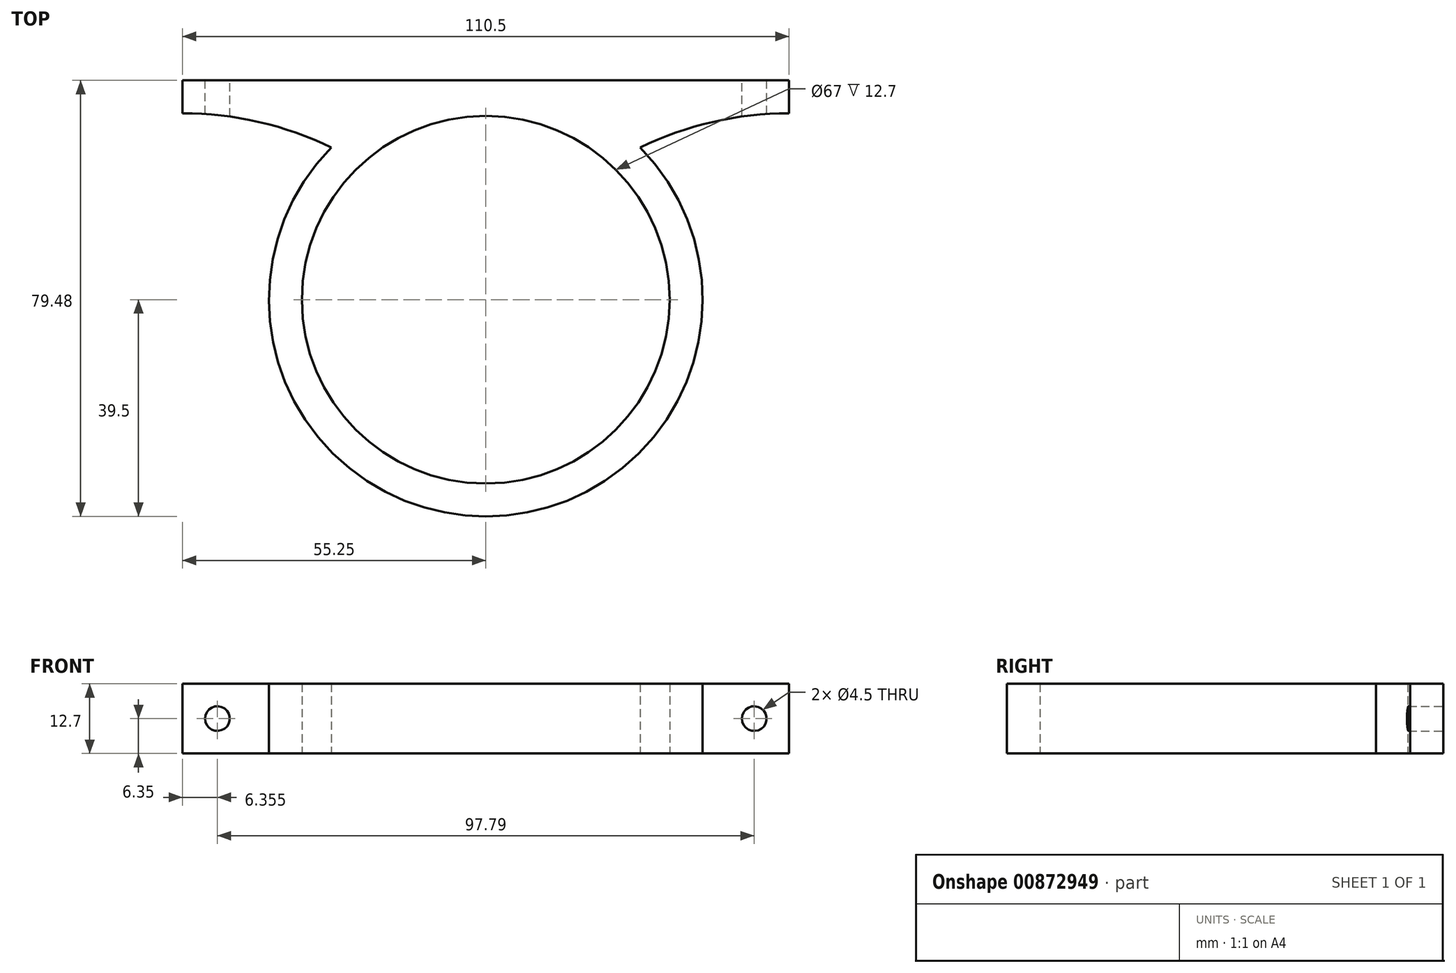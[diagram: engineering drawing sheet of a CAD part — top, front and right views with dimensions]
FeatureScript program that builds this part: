
annotation { "Feature Type Name" : "Feature", "Feature Type Description" : "" }
export const myFeature = defineFeature(function(context is Context, id is Id, definition is map)
    precondition{}
    {
        {
            var Q0;
            Q0=qCreatedBy(makeId("Top.planeOp"),FACE);
            var sketch = newSketch(context, id + "F0", { "sketchPlane" : qUnion([Q0])});
            skCircle(sketch, "E0", {"center": v(0, 0) * mm, "radius": 33.5 * mm});
            skCircle(sketch, "E1", {"center": v(0, 0) * mm, "radius": 39.5 * mm});
            skLineSegment(sketch, "E2.bottom", {"start": v(55.25, 33.98) * mm, "end": v(-55.25, 33.98) * mm});
            skLineSegment(sketch, "E2.top", {"start": v(55.25, 39.98) * mm, "end": v(-55.25, 39.98) * mm});
            skLineSegment(sketch, "E2.left", {"start": v(55.25, 33.98) * mm, "end": v(55.25, 39.98) * mm});
            skLineSegment(sketch, "E2.right", {"start": v(-55.25, 33.98) * mm, "end": v(-55.25, 39.98) * mm});
            skPoint(sketch, "E2.middle", {"position": v(0, 36.98) * mm});
            skArc(sketch, "E3", {"start": v(0, 0) * mm, "mid": v(-22.81, 24.8) * mm, "end": v(-55.24, 33.98) * mm});
            skArc(sketch, "E4", {"start": v(55.25, 33.98) * mm, "mid": v(22.81, 24.8) * mm, "end": v(0, 0) * mm});
            skSolve(sketch);
        }
        {
            var Q0;
            Q0=makeQuery(id+"F0.imprint","IMPRINT",FACE,{"disambiguationData":[TD([[makeQuery(id+"F0.imprint","IMPRINT",EDGE,{"derivedFrom":sQuery(id+"F0.wireOp",EDGE,"E2.top")}),1.0]])]});
            var Q1;
            {var subQ0=sQuery(id+"F0.wireOp",EDGE,"E3");var subQ1=sQuery(id+"F0.wireOp",EDGE,"E1");var subQ2=makeQuery(id+"F0.imprint","INTERSECT",VERTEX,{"derivedFrom":[subQ1,subQ0]});Q1=makeQuery(id+"F0.imprint","IMPRINT",FACE,{"disambiguationData":[TD([[makeQuery(id+"F0.imprint","IMPRINT",EDGE,{"disambiguationData":[TD([[subQ2,1.0]])],"derivedFrom":subQ1}),-1.0]])]});}
            var Q2;
            {var subQ0=sQuery(id+"F0.wireOp",EDGE,"E3");var subQ8=sQuery(id+"F0.wireOp",EDGE,"E0");var subQ9=makeQuery(id+"F0.imprint","INTERSECT",VERTEX,{"derivedFrom":[subQ8,subQ0]});Q2=makeQuery(id+"F0.imprint","IMPRINT",FACE,{"disambiguationData":[TD([[makeQuery(id+"F0.imprint","IMPRINT",EDGE,{"disambiguationData":[TD([[subQ9,1.0]])],"derivedFrom":subQ8}),-1.0]])]});}
            var Q3;
            {var subQ0=sQuery(id+"F0.wireOp",EDGE,"E2.bottom");var subQ1=sQuery(id+"F0.wireOp",EDGE,"E1");var subQ2=makeQuery(id+"F0.imprint","INTERSECT",VERTEX,{"disambiguationData":[OD(0.0)],"derivedFrom":[subQ1,subQ0]});Q3=makeQuery(id+"F0.imprint","IMPRINT",FACE,{"disambiguationData":[TD([[makeQuery(id+"F0.imprint","IMPRINT",EDGE,{"disambiguationData":[TD([[subQ2,-1.0]])],"derivedFrom":subQ1}),1.0]])]});}
            var Q4;
            {var subQ0=sQuery(id+"F0.wireOp",EDGE,"E4");var subQ1=sQuery(id+"F0.wireOp",EDGE,"E1");var subQ2=makeQuery(id+"F0.imprint","INTERSECT",VERTEX,{"derivedFrom":[subQ1,subQ0]});Q4=makeQuery(id+"F0.imprint","IMPRINT",FACE,{"disambiguationData":[TD([[makeQuery(id+"F0.imprint","IMPRINT",EDGE,{"disambiguationData":[TD([[subQ2,-1.0]])],"derivedFrom":subQ1}),-1.0]])]});}
            var Q5;
            {var subQ0=sQuery(id+"F0.wireOp",EDGE,"E3");var subQ1=sQuery(id+"F0.wireOp",EDGE,"E0");var subQ2=makeQuery(id+"F0.imprint","INTERSECT",VERTEX,{"derivedFrom":[subQ1,subQ0]});Q5=makeQuery(id+"F0.imprint","IMPRINT",FACE,{"disambiguationData":[TD([[makeQuery(id+"F0.imprint","IMPRINT",EDGE,{"disambiguationData":[TD([[subQ2,-1.0]])],"derivedFrom":subQ1}),-1.0]])]});}
            extrude(context, id + "F1", {"entities" : qUnion([Q0, Q1, Q2, Q3, Q4, Q5]), "depth" : 12.7 * mm, "offsetDistance" : 25.4 * mm});
        }
        {
            var Q0;
            Q0=makeQuery(id+"F1.opExtrude","SWEPT_FACE",FACE,{"disambiguationData":[OSD([sQuery(id+"F0.wireOp",EDGE,"E2.top")])]});
            var sketch = newSketch(context, id + "F2", { "sketchPlane" : qUnion([Q0])});
            skCircle(sketch, "E5", {"center": v(-48.9, 6.35) * mm, "radius": 2.25 * mm});
            skCircle(sketch, "E6", {"center": v(48.9, 6.35) * mm, "radius": 2.25 * mm});
            skSolve(sketch);
        }
        {
            var Q0;
            Q0=makeQuery(id+"F2.imprint","IMPRINT",FACE,{"disambiguationData":[TD([[makeQuery(id+"F2.imprint","IMPRINT",EDGE,{"derivedFrom":sQuery(id+"F2.wireOp",EDGE,"E5")}),1.0]])]});
            var Q1;
            Q1=makeQuery(id+"F2.imprint","IMPRINT",FACE,{"disambiguationData":[TD([[makeQuery(id+"F2.imprint","IMPRINT",EDGE,{"derivedFrom":sQuery(id+"F2.wireOp",EDGE,"E6")}),1.0]])]});
            extrude(context, id + "F3", {"entities" : qUnion([Q0, Q1]), "operationType" : NewBodyOperationType.REMOVE, "endBound" : BoundingType.UP_TO_NEXT, "oppositeDirection" : true, "depth" : 25.4 * mm, "offsetDistance" : 25.4 * mm});
        }
    });
